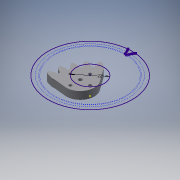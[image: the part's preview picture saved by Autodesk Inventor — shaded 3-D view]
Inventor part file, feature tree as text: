
AUTODESK INVENTOR PART (.ipt)
format: ipt  version: 2017 (Build 210142000, 142)  size: 445,440 bytes
history: native  units: mm
features: sketch x8, extrude x6, pattern_circular x1, projected_geometry x1
ambient origin geometry x8: Origin, YZ Plane, XZ Plane, XY Plane, X Axis, Y Axis, Z Axis, Center Point
bodies: Solide1 (feature_tree)
feature tree (16):
  sketch  "Sketch1"  dims[d0=20.0mm d1=0.0mm d2=26.5mm d3=0.0mm d4=260.0mm d5=360.0deg d7=14.0mm d8=0.0mm d9=10.0mm d10=9.424778mm d11=36.0mm d13=50.0mm d15=40.0mm d16=22.0mm d17=7.75mm d18=2.3mm d19=3.9mm d20=360.0deg d23=22.0mm d24=22.0mm d25=10.0mm d26=0.0mm d47=10.0mm d48=0.0mm d50=40.0mm d51=22.0mm d52=7.75mm d53=2.3mm d54=3.9mm d55=360.0deg d57=40.0mm d59=7.75mm d60=2.3mm d61=3.9mm d62=360.0deg d63=2.7mm d64=10.0mm d65=0.0mm]
  extrude  "Extrusion1"  TaperAngle=0.0deg  [1 undecoded]
  extrude  "Extrusion2"  Depth=10.0mm TaperAngle=0.0deg
  pattern_circular  "Réseau circulaire1"  Count=26 Angle=360.0deg
  extrude  "Extrusion3"  Depth=14.0mm TaperAngle=0.0deg
  sketch  "Esquisse3"
  extrude  "Extrusion5"  Depth=10.0mm
  sketch  "Esquisse5"
  extrude  "Extrusion6"  Depth=10.0mm
  sketch  "Esquisse7"
  extrude  "Extrusion7"  Depth=10.0mm
  sketch  "Esquisse9"
  sketch  "Esquisse2"
  projected_geometry  "Boucle projetée1"
  sketch  "Esquisse4"
  sketch  "Esquisse8"
note: 1 required parameter value undecoded (feature->parameter linkage not recoverable at this tier; creation-order binding heuristic only, values carry confidence <= 0.55)
